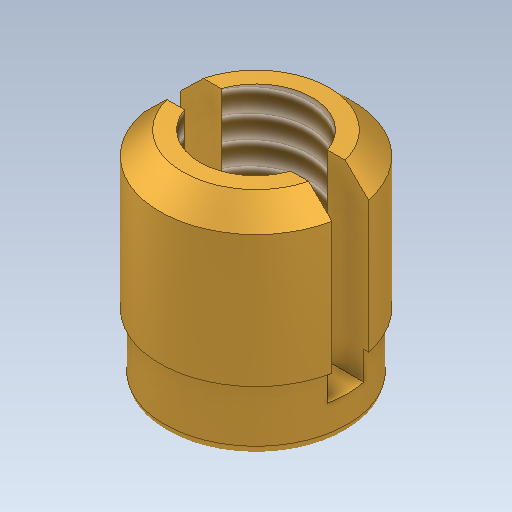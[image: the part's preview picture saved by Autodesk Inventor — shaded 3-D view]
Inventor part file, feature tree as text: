
AUTODESK INVENTOR PART (.ipt)
format: ipt  version: 2021 (Build 250183000, 183)  size: 196,608 bytes
history: native  units: mm
features: sketch x3, extrude x3, chamfer x2, hole x1, fillet x1
ambient origin geometry x8: Origin, YZ Plane, XZ Plane, XY Plane, X Axis, Y Axis, Z Axis, Center Point
bodies: Solid1 (feature_tree)
feature tree (10):
  sketch  "Sketch1"  dims[d0=4.2mm d1=4.78mm d2=0.0mm]
  extrude  "Extrusion1"  Depth=4.78mm TaperAngle=0.0deg
  hole  "Hole1"  [1 undecoded]
  chamfer  "Chamfer1"  Distance=4.0mm
  extrude  "Extrusion2"  Depth=4.0mm
  extrude  "Extrusion3"  Depth=1.4mm TaperAngle=0.0deg
  fillet  "Fillet1"  Radius=0.2mm
  chamfer  "Chamfer2"  Distance=2.0mm Angle=45.0deg
  sketch  "Sketch2"  dims[d3=2.459mm d4=6.0mm d5=4.0mm d6=2.0mm d7=90.0deg d8=8.8mm d9=20.594885mm d10=0.5mm d11=2.0mm d12=45.0deg]
  sketch  "Sketch3"  dims[d13=0.8mm d14=4.0mm d15=0.0mm d16=4.0mm d17=1.4mm d18=0.0mm d19=0.2mm d20=0.3mm d21=2.0mm d22=45.0deg]
note: 1 required parameter value undecoded (feature->parameter linkage not recoverable at this tier; creation-order binding heuristic only, values carry confidence <= 0.55)
